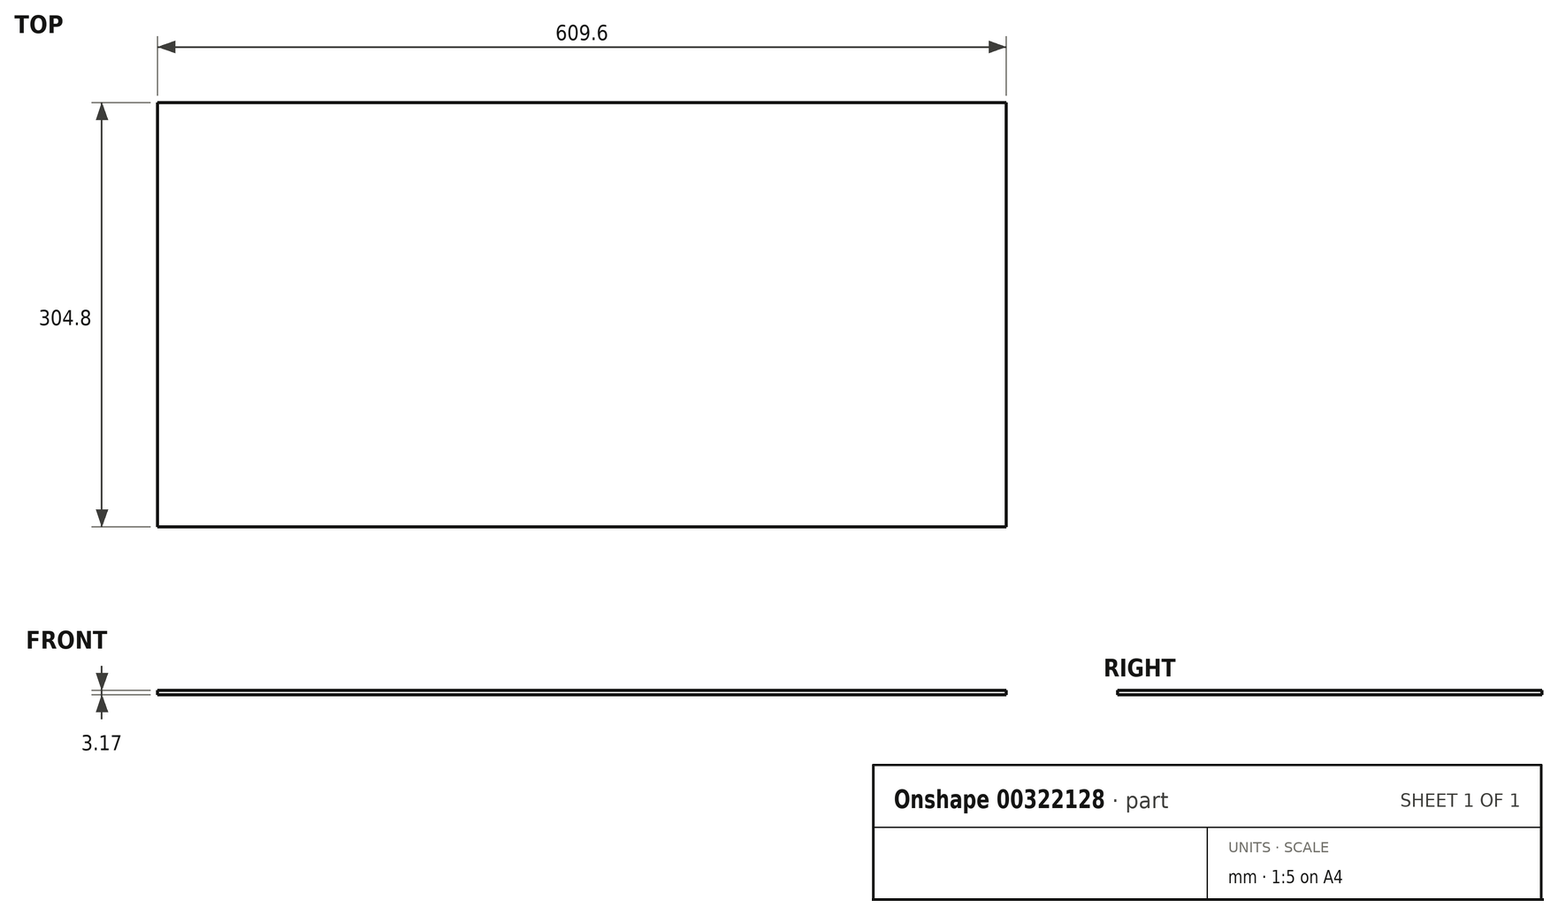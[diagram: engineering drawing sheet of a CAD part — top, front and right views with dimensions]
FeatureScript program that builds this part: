
annotation { "Feature Type Name" : "Feature", "Feature Type Description" : "" }
export const myFeature = defineFeature(function(context is Context, id is Id, definition is map)
    precondition{}
    {
        {
            var Q0;
            Q0=qCreatedBy(makeId("Top.planeOp"),FACE);
            var sketch = newSketch(context, id + "F0", { "sketchPlane" : qUnion([Q0])});
            skLineSegment(sketch, "E0.bottom", {"start": v(-304.8, 152.4) * mm, "end": v(304.8, 152.4) * mm});
            skLineSegment(sketch, "E0.top", {"start": v(-304.8, -152.4) * mm, "end": v(304.8, -152.4) * mm});
            skLineSegment(sketch, "E0.left", {"start": v(-304.8, 152.4) * mm, "end": v(-304.8, -152.4) * mm});
            skLineSegment(sketch, "E0.right", {"start": v(304.8, 152.4) * mm, "end": v(304.8, -152.4) * mm});
            skPoint(sketch, "E0.middle", {"position": v(0, 0) * mm});
            skSolve(sketch);
        }
        {
            var Q0;
            Q0=makeQuery(id+"F0.imprint","IMPRINT",FACE,{"disambiguationData":[TD([[makeQuery(id+"F0.imprint","IMPRINT",EDGE,{"derivedFrom":sQuery(id+"F0.wireOp",EDGE,"E0.bottom")}),-1.0]])]});
            extrude(context, id + "F1", {"entities" : qUnion([Q0]), "depth" : 3.17 * mm});
        }
    });
